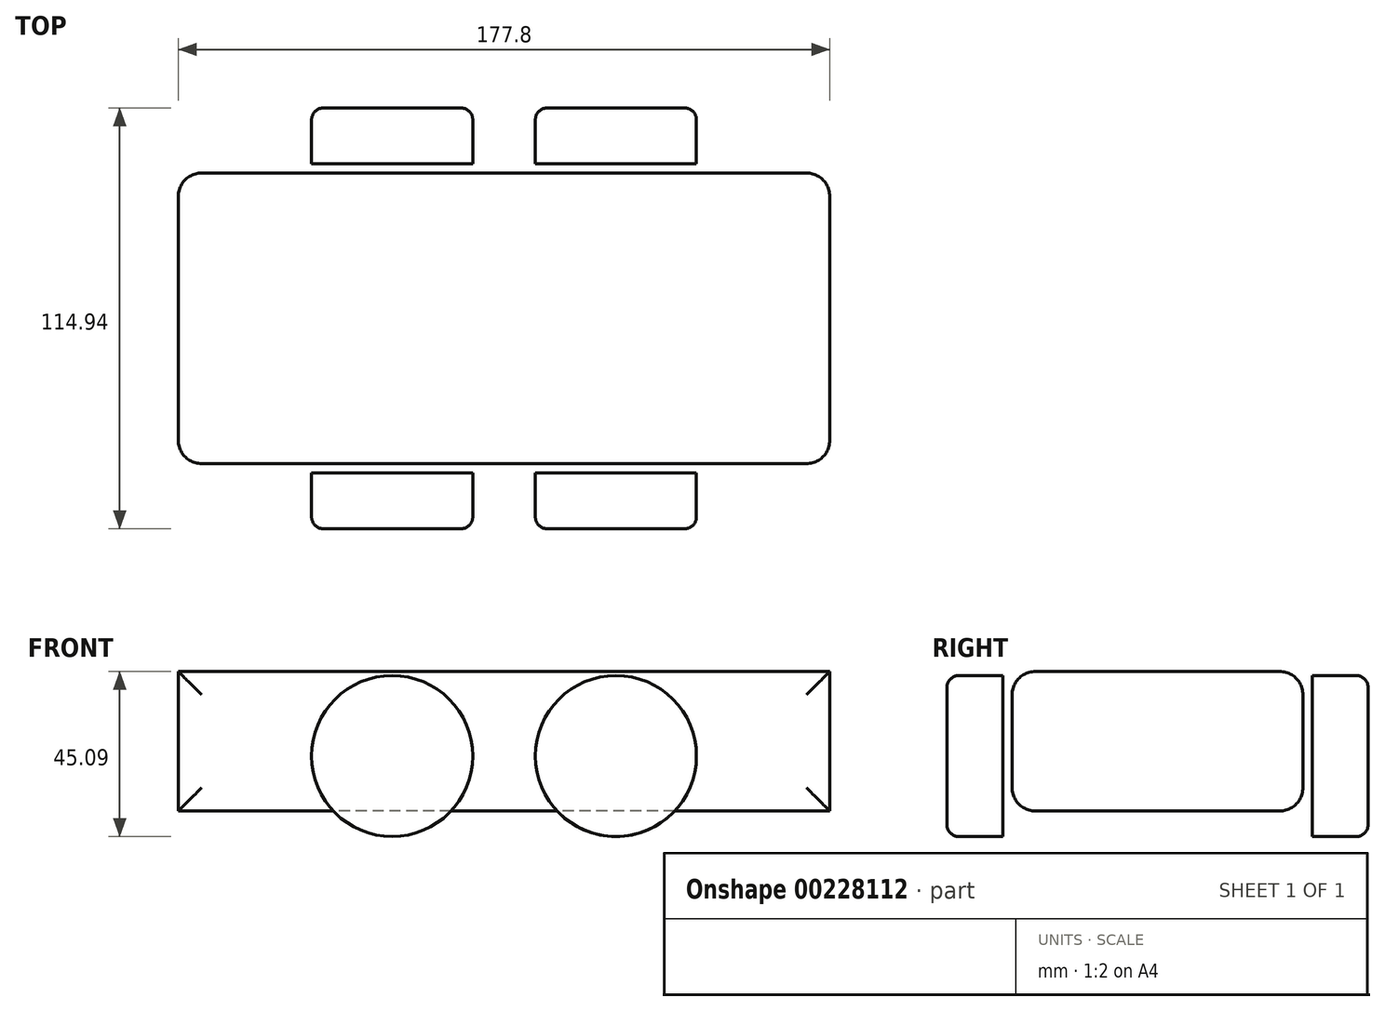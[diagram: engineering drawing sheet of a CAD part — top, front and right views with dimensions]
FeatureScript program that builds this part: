
annotation { "Feature Type Name" : "Feature", "Feature Type Description" : "" }
export const myFeature = defineFeature(function(context is Context, id is Id, definition is map)
    precondition{}
    {
        {
            var Q0;
            Q0=qCreatedBy(makeId("Front.planeOp"),FACE);
            var sketch = newSketch(context, id + "F0", { "sketchPlane" : qUnion([Q0])});
            skLineSegment(sketch, "E0.bottom", {"start": v(88.9, -19.05) * mm, "end": v(-88.9, -19.05) * mm});
            skLineSegment(sketch, "E0.top", {"start": v(88.9, 19.05) * mm, "end": v(-88.9, 19.05) * mm});
            skLineSegment(sketch, "E0.left", {"start": v(88.9, -19.05) * mm, "end": v(88.9, 19.05) * mm});
            skLineSegment(sketch, "E0.right", {"start": v(-88.9, -19.05) * mm, "end": v(-88.9, 19.05) * mm});
            skPoint(sketch, "E0.middle", {"position": v(0, 0) * mm});
            skLineSegment(sketch, "E1", {"start": v(-127.75, -26.04) * mm, "end": v(100.64, -26.04) * mm, "construction": true});
            skSolve(sketch);
        }
        {
            var Q0;
            Q0=makeQuery(id+"F0.imprint","IMPRINT",FACE,{"disambiguationData":[TD([[makeQuery(id+"F0.imprint","IMPRINT",EDGE,{"derivedFrom":sQuery(id+"F0.wireOp",EDGE,"E0.bottom")}),-1.0]])]});
            var sketch = newSketch(context, id + "F1", { "sketchPlane" : qUnion([Q0])});
            skSolve(sketch);
        }
        {
            var Q0;
            Q0=makeQuery(id+"F0.imprint","IMPRINT",FACE,{"disambiguationData":[TD([[makeQuery(id+"F0.imprint","IMPRINT",EDGE,{"derivedFrom":sQuery(id+"F0.wireOp",EDGE,"E0.bottom")}),-1.0]])]});
            var sketch = newSketch(context, id + "F2", { "sketchPlane" : qUnion([Q0])});
            skCircle(sketch, "E2", {"center": v(30.54, -4.06) * mm, "radius": 21.98 * mm});
            skSolve(sketch);
        }
        {
            var Q0;
            Q0=makeQuery(id+"F1.imprint","IMPRINT",FACE,{"disambiguationData":[TD([[makeQuery(id+"F1.imprint","IMPRINT",EDGE,{"derivedFrom":makeQuery(id+"F0.imprint","IMPRINT",EDGE,{"derivedFrom":sQuery(id+"F0.wireOp",EDGE,"E0.bottom")})}),-1.0]])]});
            extrude(context, id + "F3", {"entities" : qUnion([Q0]), "endBound" : BoundingType.SYMMETRIC, "depth" : 79.38 * mm});
        }
        {
            var Q0;
            Q0=makeQuery(id+"F3.opExtrude","CAP_FACE",FACE,{"disambiguationData":[OSD([sQuery(id+"F0.wireOp",EDGE,"E0.bottom"),sQuery(id+"F0.wireOp",EDGE,"E0.top"),sQuery(id+"F0.wireOp",EDGE,"E0.left"),sQuery(id+"F0.wireOp",EDGE,"E0.right")])],"isStart":false});
            cPlane(context, id + "F4", {"entities" : qUnion([Q0]), "cplaneType" : CPlaneType.OFFSET, "offset" : 2.54 * mm, "width" : 152.4 * mm, "height" : 152.4 * mm});
        }
        {
            var Q0;
            Q0=qCreatedBy(id+"F4.planeOp",FACE);
            var sketch = newSketch(context, id + "F5", { "sketchPlane" : qUnion([Q0])});
            skCircle(sketch, "E3.0", {"center": v(30.54, -4.06) * mm, "radius": 21.98 * mm});
            skSolve(sketch);
        }
        {
            var Q0;
            Q0=makeQuery(id+"F5.imprint","IMPRINT",FACE,{"disambiguationData":[TD([[makeQuery(id+"F5.imprint","IMPRINT",EDGE,{"derivedFrom":sQuery(id+"F5.wireOp",EDGE,"E3.0")}),1.0]])]});
            var Q1;
            Q1=sQuery(id+"F5.wireOp",EDGE,"E3.0");
            extrude(context, id + "F6", {"entities" : qUnion([Q0]), "surfaceEntities" : qUnion([Q1]), "depth" : 15.24 * mm});
        }
        {
            var Q0;
            Q0=makeQuery(id+"F6.opExtrude","CAP_EDGE",EDGE,{"disambiguationData":[OSD([sQuery(id+"F5.wireOp",EDGE,"E3.0")])],"isStart":false});
            fillet(context, id + "F7", {"entities" : qUnion([Q0]), "radius" : 3.17 * mm, "tangentPropagation" : true, "allowEdgeOverflow" : false});
        }
        {
            var Q0;
            Q0=makeQuery(id+"F3.opExtrude","CAP_EDGE",EDGE,{"disambiguationData":[OSD([sQuery(id+"F0.wireOp",EDGE,"E0.top")])],"isStart":false});
            var Q1;
            Q1=makeQuery(id+"F3.opExtrude","CAP_EDGE",EDGE,{"disambiguationData":[OSD([sQuery(id+"F0.wireOp",EDGE,"E0.right")])],"isStart":false});
            var Q2;
            Q2=makeQuery(id+"F3.opExtrude","CAP_EDGE",EDGE,{"disambiguationData":[OSD([sQuery(id+"F0.wireOp",EDGE,"E0.bottom")])],"isStart":false});
            var Q3;
            Q3=makeQuery(id+"F3.opExtrude","CAP_EDGE",EDGE,{"disambiguationData":[OSD([sQuery(id+"F0.wireOp",EDGE,"E0.left")])],"isStart":false});
            var Q4;
            Q4=makeQuery(id+"F3.opExtrude","CAP_EDGE",EDGE,{"disambiguationData":[OSD([sQuery(id+"F0.wireOp",EDGE,"E0.left")])],"isStart":true});
            var Q5;
            Q5=makeQuery(id+"F3.opExtrude","CAP_EDGE",EDGE,{"disambiguationData":[OSD([sQuery(id+"F0.wireOp",EDGE,"E0.top")])],"isStart":true});
            var Q6;
            Q6=makeQuery(id+"F3.opExtrude","CAP_EDGE",EDGE,{"disambiguationData":[OSD([sQuery(id+"F0.wireOp",EDGE,"E0.bottom")])],"isStart":true});
            var Q7;
            Q7=makeQuery(id+"F3.opExtrude","CAP_EDGE",EDGE,{"disambiguationData":[OSD([sQuery(id+"F0.wireOp",EDGE,"E0.right")])],"isStart":true});
            fillet(context, id + "F8", {"entities" : qUnion([Q0, Q1, Q2, Q3, Q4, Q5, Q6, Q7]), "radius" : 6.35 * mm, "tangentPropagation" : true, "allowEdgeOverflow" : false});
        }
        {
            var Q0;
            Q0=makeQuery(id+"F6.opExtrude","SWEPT_BODY",BODY,{"disambiguationData":[OSD([sQuery(id+"F5.wireOp",EDGE,"E3.0")])]});
            var Q1;
            Q1=qCreatedBy(makeId("Front.planeOp"),FACE);
            mirror(context, id + "F9", {"entities" : qUnion([Q0]), "mirrorPlane" : qUnion([Q1])});
        }
        {
            var Q0;
            Q0=makeQuery(id+"F6.opExtrude","SWEPT_BODY",BODY,{"disambiguationData":[OSD([sQuery(id+"F5.wireOp",EDGE,"E3.0")])]});
            var Q1;
            Q1=makeQuery(id+"F9.opPattern","COPY",BODY,{"derivedFrom":makeQuery(id+"F6.opExtrude","SWEPT_BODY",BODY,{"disambiguationData":[OSD([sQuery(id+"F5.wireOp",EDGE,"E3.0")])]}),"instanceName":"1"});
            var Q2;
            Q2=qCreatedBy(makeId("Right.planeOp"),FACE);
            mirror(context, id + "F10", {"entities" : qUnion([Q0, Q1]), "mirrorPlane" : qUnion([Q2])});
        }
        {
            var Q0;
            Q0=qCreatedBy(makeId("Front.planeOp"),FACE);
            var sketch = newSketch(context, id + "F11", { "sketchPlane" : qUnion([Q0])});
            skLineSegment(sketch, "E4", {"start": v(-61.1, 19.05) * mm, "end": v(-16.19, 37.2) * mm});
            skArc(sketch, "E5", {"start": v(57.92, 19.05) * mm, "mid": v(23.8, 40.1) * mm, "end": v(-16.19, 37.2) * mm});
            skSolve(sketch);
        }
        {
            var Q0;
            Q0 = qSketchRegion(id + "F11", true);
            var Q1;
            Q1=sQuery(id+"F11.wireOp",EDGE,"E5");
            var Q2;
            Q2=sQuery(id+"F11.wireOp",EDGE,"E4");
            extrude(context, id + "F12", {"entities" : qUnion([Q0]), "bodyType" : ToolBodyType.SURFACE, "surfaceEntities" : qUnion([Q1, Q2]), "endBound" : BoundingType.SYMMETRIC, "oppositeDirection" : true, "depth" : 57.15 * mm});
        }
    });
